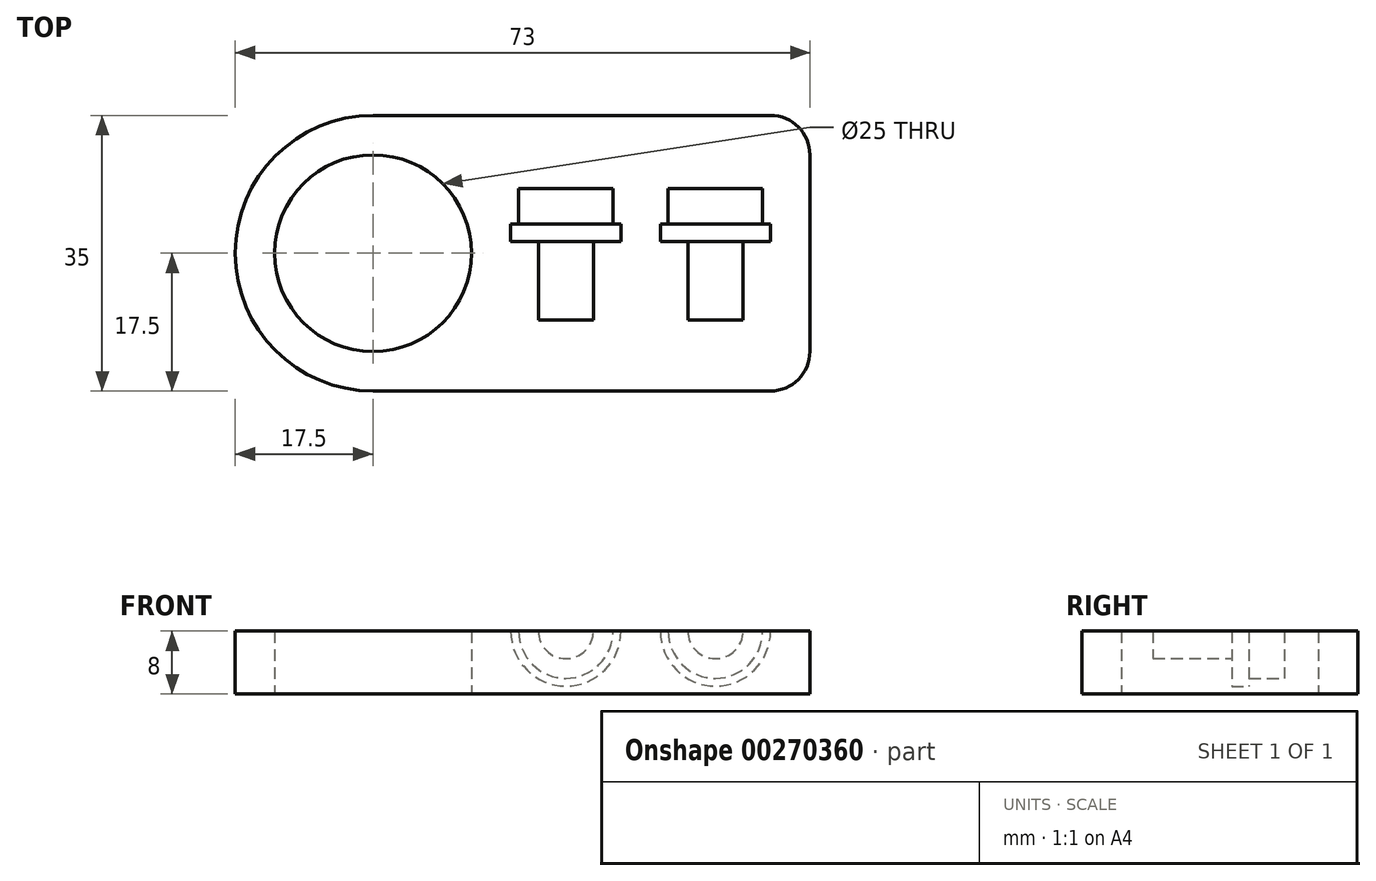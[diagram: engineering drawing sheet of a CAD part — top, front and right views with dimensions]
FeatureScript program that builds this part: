
annotation { "Feature Type Name" : "Feature", "Feature Type Description" : "" }
export const myFeature = defineFeature(function(context is Context, id is Id, definition is map)
    precondition{}
    {
        {
            var Q0;
            Q0=qCreatedBy(makeId("Top.planeOp"),FACE);
            var sketch = newSketch(context, id + "F0", { "sketchPlane" : qUnion([Q0])});
            skLineSegment(sketch, "E0.bottom", {"start": v(17.5, 0) * mm, "end": v(68, 0) * mm});
            skLineSegment(sketch, "E0.top", {"start": v(17.5, 35) * mm, "end": v(68, 35) * mm});
            skLineSegment(sketch, "E0.left", {"start": v(0, 17.5) * mm, "end": v(0, 17.5) * mm});
            skLineSegment(sketch, "E0.right", {"start": v(73, 5) * mm, "end": v(73, 30) * mm});
            skLineSegment(sketch, "E1.bottom", {"start": v(0, 0) * mm, "end": v(17.5, 0) * mm, "construction": true});
            skLineSegment(sketch, "E1.top", {"start": v(0, 17.5) * mm, "end": v(17.5, 17.5) * mm, "construction": true});
            skLineSegment(sketch, "E1.left", {"start": v(0, 0) * mm, "end": v(0, 17.5) * mm, "construction": true});
            skLineSegment(sketch, "E1.right", {"start": v(17.5, 0) * mm, "end": v(17.5, 17.5) * mm, "construction": true});
            skCircle(sketch, "E2", {"center": v(17.5, 17.5) * mm, "radius": 12.5 * mm});
            skPoint(sketch, "E3.visualSharp", {"position": v(0, 0) * mm});
            skArc(sketch, "E3.filletArc", {"start": v(0, 17.5) * mm, "mid": v(5.13, 5.13) * mm, "end": v(17.5, 0) * mm});
            skPoint(sketch, "E4.visualSharp", {"position": v(0, 35) * mm});
            skArc(sketch, "E4.filletArc", {"start": v(17.5, 35) * mm, "mid": v(5.13, 29.87) * mm, "end": v(0, 17.5) * mm});
            skPoint(sketch, "E5.visualSharp", {"position": v(73, 35) * mm});
            skArc(sketch, "E5.filletArc", {"start": v(73, 30) * mm, "mid": v(71.54, 33.54) * mm, "end": v(68, 35) * mm});
            skPoint(sketch, "E6.visualSharp", {"position": v(73, 0) * mm});
            skArc(sketch, "E6.filletArc", {"start": v(68, 0) * mm, "mid": v(71.54, 1.46) * mm, "end": v(73, 5) * mm});
            skSolve(sketch);
        }
        {
            var Q0;
            Q0=makeQuery(id+"F0.imprint","IMPRINT",FACE,{"disambiguationData":[TD([[makeQuery(id+"F0.imprint","IMPRINT",EDGE,{"derivedFrom":sQuery(id+"F0.wireOp",EDGE,"E0.bottom")}),1.0]])]});
            extrude(context, id + "F1", {"entities" : qUnion([Q0]), "depth" : 8 * mm});
        }
        {
            var Q0;
            Q0=makeQuery(id+"F1.opExtrude","CAP_FACE",FACE,{"disambiguationData":[OSD([sQuery(id+"F0.wireOp",EDGE,"E0.bottom"),sQuery(id+"F0.wireOp",EDGE,"E0.top"),sQuery(id+"F0.wireOp",EDGE,"E0.right"),sQuery(id+"F0.wireOp",EDGE,"E2"),sQuery(id+"F0.wireOp",EDGE,"E3.filletArc"),sQuery(id+"F0.wireOp",EDGE,"E4.filletArc"),sQuery(id+"F0.wireOp",EDGE,"E5.filletArc"),sQuery(id+"F0.wireOp",EDGE,"E6.filletArc")])],"isStart":false});
            var sketch = newSketch(context, id + "F2", { "sketchPlane" : qUnion([Q0])});
            skLineSegment(sketch, "E7.bottom", {"start": v(0, 0) * mm, "end": v(42, 0) * mm, "construction": true});
            skLineSegment(sketch, "E7.top", {"start": v(0, 9) * mm, "end": v(42, 9) * mm, "construction": true});
            skLineSegment(sketch, "E7.left", {"start": v(0, 0) * mm, "end": v(0, 9) * mm, "construction": true});
            skLineSegment(sketch, "E7.right", {"start": v(42, 0) * mm, "end": v(42, 9) * mm, "construction": true});
            skLineSegment(sketch, "E8.bottom", {"start": v(42, 9) * mm, "end": v(45.5, 9) * mm});
            skLineSegment(sketch, "E8.left", {"start": v(42, 9) * mm, "end": v(42, 19) * mm});
            skLineSegment(sketch, "E8.right", {"start": v(45.5, 9) * mm, "end": v(45.5, 19) * mm});
            skLineSegment(sketch, "E9.bottom", {"start": v(45.5, 19) * mm, "end": v(49, 19) * mm});
            skLineSegment(sketch, "E9.top", {"start": v(48, 21.2) * mm, "end": v(49, 21.2) * mm});
            skLineSegment(sketch, "E9.left", {"start": v(42, 19) * mm, "end": v(42, 21.2) * mm});
            skLineSegment(sketch, "E9.right", {"start": v(49, 19) * mm, "end": v(49, 21.2) * mm});
            skLineSegment(sketch, "E10.top", {"start": v(42, 25.7) * mm, "end": v(48, 25.7) * mm});
            skLineSegment(sketch, "E10.left", {"start": v(42, 21.2) * mm, "end": v(42, 25.7) * mm});
            skLineSegment(sketch, "E10.right", {"start": v(48, 21.2) * mm, "end": v(48, 25.7) * mm});
            skLineSegment(sketch, "E11", {"start": v(42, 9) * mm, "end": v(61, 9) * mm, "construction": true});
            skLineSegment(sketch, "E12.bottom", {"start": v(61, 9) * mm, "end": v(64.5, 9) * mm});
            skLineSegment(sketch, "E12.left", {"start": v(61, 9) * mm, "end": v(61, 19) * mm});
            skLineSegment(sketch, "E12.right", {"start": v(64.5, 9) * mm, "end": v(64.5, 19) * mm});
            skLineSegment(sketch, "E13.bottom", {"start": v(64.5, 19) * mm, "end": v(68, 19) * mm});
            skLineSegment(sketch, "E13.top", {"start": v(67, 21.2) * mm, "end": v(68, 21.2) * mm});
            skLineSegment(sketch, "E13.left", {"start": v(61, 19) * mm, "end": v(61, 21.2) * mm});
            skLineSegment(sketch, "E13.right", {"start": v(68, 19) * mm, "end": v(68, 21.2) * mm});
            skLineSegment(sketch, "E14.top", {"start": v(61, 25.7) * mm, "end": v(67, 25.7) * mm});
            skLineSegment(sketch, "E14.left", {"start": v(61, 21.2) * mm, "end": v(61, 25.7) * mm});
            skLineSegment(sketch, "E14.right", {"start": v(67, 21.2) * mm, "end": v(67, 25.7) * mm});
            skSolve(sketch);
        }
        {
            var Q0;
            Q0=makeQuery(id+"F2.imprint","IMPRINT",FACE,{"disambiguationData":[TD([[makeQuery(id+"F2.imprint","IMPRINT",EDGE,{"derivedFrom":sQuery(id+"F2.wireOp",EDGE,"E8.bottom")}),1.0]])]});
            var Q1;
            Q1=sQuery(id+"F2.wireOp",EDGE,"E8.left");
            revolve(context, id + "F3", {"operationType" : NewBodyOperationType.REMOVE, "entities" : qUnion([Q0]), "axis" : qUnion([Q1]), "revolveType" : RevolveType.FULL, "oppositeDirection" : true});
        }
        {
            var Q0;
            Q0=makeQuery(id+"F2.imprint","IMPRINT",FACE,{"disambiguationData":[TD([[makeQuery(id+"F2.imprint","IMPRINT",EDGE,{"derivedFrom":sQuery(id+"F2.wireOp",EDGE,"E12.bottom")}),1.0]])]});
            var Q1;
            Q1=sQuery(id+"F2.wireOp",EDGE,"E12.left");
            revolve(context, id + "F4", {"operationType" : NewBodyOperationType.REMOVE, "entities" : qUnion([Q0]), "axis" : qUnion([Q1]), "revolveType" : RevolveType.FULL, "oppositeDirection" : true});
        }
    });
